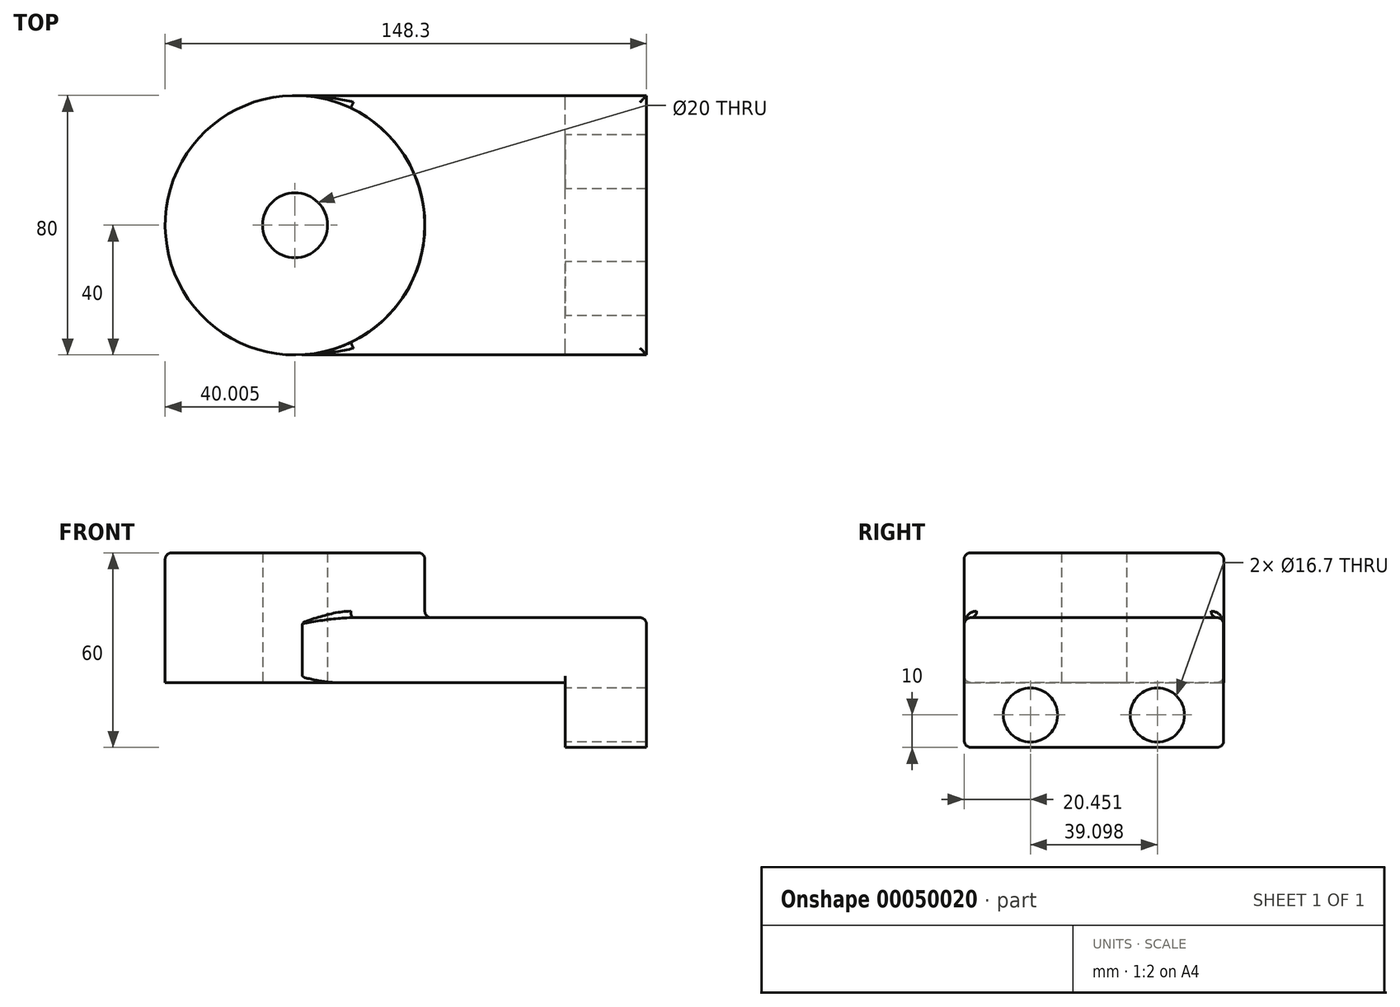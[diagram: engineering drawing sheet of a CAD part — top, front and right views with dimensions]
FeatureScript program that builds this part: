
annotation { "Feature Type Name" : "Feature", "Feature Type Description" : "" }
export const myFeature = defineFeature(function(context is Context, id is Id, definition is map)
    precondition{}
    {
        {
            var Q0;
            Q0=qCreatedBy(makeId("Top.planeOp"),FACE);
            var sketch = newSketch(context, id + "F0", { "sketchPlane" : qUnion([Q0])});
            skLineSegment(sketch, "E0.rect.bottom", {"start": v(41.65, -39.94) * mm, "end": v(-41.65, -39.94) * mm});
            skLineSegment(sketch, "E0.rect.top", {"start": v(41.65, 39.94) * mm, "end": v(-41.65, 39.94) * mm});
            skLineSegment(sketch, "E0.rect.left", {"start": v(41.65, -39.94) * mm, "end": v(41.65, 39.94) * mm});
            skLineSegment(sketch, "E0.rect.right", {"start": v(-41.65, -39.94) * mm, "end": v(-41.65, 39.94) * mm});
            skPoint(sketch, "E0.rect.middle", {"position": v(0, 0) * mm});
            skCircle(sketch, "E1", {"center": v(-41.65, 0) * mm, "radius": 40 * mm});
            skCircle(sketch, "E2", {"center": v(-41.65, 0) * mm, "radius": 10 * mm});
            skSolve(sketch);
        }
        {
            var Q0;
            {var subQ0=sQuery(id+"F0.wireOp",EDGE,"E0.rect.left");Q0=makeQuery(id+"F0.imprint","IMPRINT",FACE,{"disambiguationData":[TD([[makeQuery(id+"F0.imprint","IMPRINT",EDGE,{"derivedFrom":subQ0}),1.0]])]});}
            var Q1;
            {var subQ0=sQuery(id+"F0.wireOp",EDGE,"E0.rect.right");var subQ5=sQuery(id+"F0.wireOp",EDGE,"E0.rect.bottom");var subQ6=makeQuery(id+"F0.imprint","INTERSECT",VERTEX,{"derivedFrom":[subQ5,subQ0]});Q1=makeQuery(id+"F0.imprint","IMPRINT",FACE,{"disambiguationData":[TD([[makeQuery(id+"F0.imprint","IMPRINT",EDGE,{"disambiguationData":[TD([[subQ6,1.0]])],"derivedFrom":subQ5}),1.0]])]});}
            var Q2;
            {var subQ0=sQuery(id+"F0.wireOp",EDGE,"E0.rect.right");var subQ5=sQuery(id+"F0.wireOp",EDGE,"E0.rect.bottom");var subQ6=makeQuery(id+"F0.imprint","INTERSECT",VERTEX,{"derivedFrom":[subQ5,subQ0]});Q2=makeQuery(id+"F0.imprint","IMPRINT",FACE,{"disambiguationData":[TD([[makeQuery(id+"F0.imprint","IMPRINT",EDGE,{"disambiguationData":[TD([[subQ6,1.0]])],"derivedFrom":subQ5}),-1.0]])]});}
            extrude(context, id + "F1", {"entities" : qUnion([Q0, Q1, Q2]), "depth" : 20 * mm});
        }
        {
            var Q0;
            {var subQ0=sQuery(id+"F0.wireOp",EDGE,"E0.rect.right");var subQ5=sQuery(id+"F0.wireOp",EDGE,"E0.rect.bottom");var subQ6=makeQuery(id+"F0.imprint","INTERSECT",VERTEX,{"derivedFrom":[subQ5,subQ0]});Q0=makeQuery(id+"F0.imprint","IMPRINT",FACE,{"disambiguationData":[TD([[makeQuery(id+"F0.imprint","IMPRINT",EDGE,{"disambiguationData":[TD([[subQ6,1.0]])],"derivedFrom":subQ5}),1.0]])]});}
            var Q1;
            {var subQ0=sQuery(id+"F0.wireOp",EDGE,"E0.rect.right");var subQ5=sQuery(id+"F0.wireOp",EDGE,"E0.rect.bottom");var subQ6=makeQuery(id+"F0.imprint","INTERSECT",VERTEX,{"derivedFrom":[subQ5,subQ0]});Q1=makeQuery(id+"F0.imprint","IMPRINT",FACE,{"disambiguationData":[TD([[makeQuery(id+"F0.imprint","IMPRINT",EDGE,{"disambiguationData":[TD([[subQ6,1.0]])],"derivedFrom":subQ5}),-1.0]])]});}
            extrude(context, id + "F2", {"entities" : qUnion([Q0, Q1]), "operationType" : NewBodyOperationType.ADD, "depth" : 40 * mm});
        }
        {
            var Q0;
            Q0=makeQuery(id+"F1.opExtrude","SWEPT_FACE",FACE,{"disambiguationData":[OSD([sQuery(id+"F0.wireOp",EDGE,"E0.rect.left")])]});
            var sketch = newSketch(context, id + "F3", { "sketchPlane" : qUnion([Q0])});
            skLineSegment(sketch, "E3.bottom", {"start": v(-39.94, 20) * mm, "end": v(39.94, 20) * mm});
            skLineSegment(sketch, "E3.top", {"start": v(-39.94, -20) * mm, "end": v(39.94, -20) * mm});
            skLineSegment(sketch, "E3.left", {"start": v(-39.94, 20) * mm, "end": v(-39.94, -20) * mm});
            skLineSegment(sketch, "E3.right", {"start": v(39.94, 20) * mm, "end": v(39.94, -20) * mm});
            skLineSegment(sketch, "E4", {"start": v(0, 20) * mm, "end": v(0, -20) * mm, "construction": true});
            skCircle(sketch, "E5", {"center": v(-19.55, -10) * mm, "radius": 8.35 * mm});
            skCircle(sketch, "E6.MirrorC", {"center": v(19.55, -10) * mm, "radius": 8.35 * mm});
            skSolve(sketch);
        }
        {
            var Q0;
            Q0 = qSketchRegion(id + "F3", true);
            extrude(context, id + "F4", {"entities" : qUnion([Q0]), "operationType" : NewBodyOperationType.ADD, "depth" : 25 * mm});
        }
        {
            var Q0;
            {var subQ0=sQuery(id+"F0.wireOp",EDGE,"E1");Q0=makeQuery(id+"F2.boolean.opBoolean","INTERSECT",EDGE,{"derivedFrom":[makeQuery(id+"F1.opExtrude","CAP_FACE",FACE,{"disambiguationData":[OSD([sQuery(id+"F0.wireOp",EDGE,"E0.rect.bottom"),sQuery(id+"F0.wireOp",EDGE,"E0.rect.top"),sQuery(id+"F0.wireOp",EDGE,"E0.rect.left"),subQ0,sQuery(id+"F0.wireOp",EDGE,"E2")])],"isStart":false}),makeQuery(id+"F2.opExtrude","SWEPT_FACE",FACE,{"disambiguationData":[OSD([subQ0])]})]});}
            var Q1;
            Q1=makeQuery(id+"F4.opExtrude","SWEPT_EDGE",EDGE,{"disambiguationData":[OSD([sQuery(id+"F3.wireOp",EDGE,"E3.top"),sQuery(id+"F3.wireOp",EDGE,"E3.left")])]});
            var Q2;
            Q2=makeQuery(id+"F4.opExtrude","SWEPT_EDGE",EDGE,{"disambiguationData":[OSD([sQuery(id+"F3.wireOp",EDGE,"E3.top"),sQuery(id+"F3.wireOp",EDGE,"E3.right")])]});
            var Q3;
            Q3=makeQuery(id+"F4.boolean.opBoolean","MERGE",EDGE,{"derivedFrom":[makeQuery(id+"F1.opExtrude","CAP_EDGE",EDGE,{"disambiguationData":[OSD([sQuery(id+"F0.wireOp",EDGE,"E0.rect.top")])],"isStart":false}),makeQuery(id+"F4.opExtrude","SWEPT_EDGE",EDGE,{"disambiguationData":[OSD([sQuery(id+"F3.wireOp",EDGE,"E3.bottom"),sQuery(id+"F3.wireOp",EDGE,"E3.right")])]})]});
            var Q4;
            Q4=makeQuery(id+"F4.boolean.opBoolean","MERGE",EDGE,{"derivedFrom":[makeQuery(id+"F1.opExtrude","CAP_EDGE",EDGE,{"disambiguationData":[OSD([sQuery(id+"F0.wireOp",EDGE,"E0.rect.bottom")])],"isStart":false}),makeQuery(id+"F4.opExtrude","SWEPT_EDGE",EDGE,{"disambiguationData":[OSD([sQuery(id+"F3.wireOp",EDGE,"E3.bottom"),sQuery(id+"F3.wireOp",EDGE,"E3.left")])]})]});
            var Q5;
            Q5=makeQuery(id+"F1.opExtrude","CAP_EDGE",EDGE,{"disambiguationData":[OSD([sQuery(id+"F0.wireOp",EDGE,"E0.rect.left")])],"isStart":true});
            var Q6;
            Q6=makeQuery(id+"F1.opExtrude","CAP_EDGE",EDGE,{"disambiguationData":[OSD([sQuery(id+"F0.wireOp",EDGE,"E0.rect.top")])],"isStart":true});
            var Q7;
            Q7=makeQuery(id+"F1.opExtrude","CAP_EDGE",EDGE,{"disambiguationData":[OSD([sQuery(id+"F0.wireOp",EDGE,"E0.rect.bottom")])],"isStart":true});
            var Q8;
            Q8=makeQuery(id+"F2.opExtrude","CAP_EDGE",EDGE,{"disambiguationData":[OSD([sQuery(id+"F0.wireOp",EDGE,"E1")])],"isStart":false});
            var Q9;
            Q9=makeQuery(id+"F4.opExtrude","CAP_EDGE",EDGE,{"disambiguationData":[OSD([sQuery(id+"F3.wireOp",EDGE,"E3.bottom")])],"isStart":false});
            fillet(context, id + "F5", {"entities" : qUnion([Q0, Q1, Q2, Q3, Q4, Q5, Q6, Q7, Q8, Q9]), "radius" : 2 * mm, "tangentPropagation" : true, "allowEdgeOverflow" : false});
        }
    });
